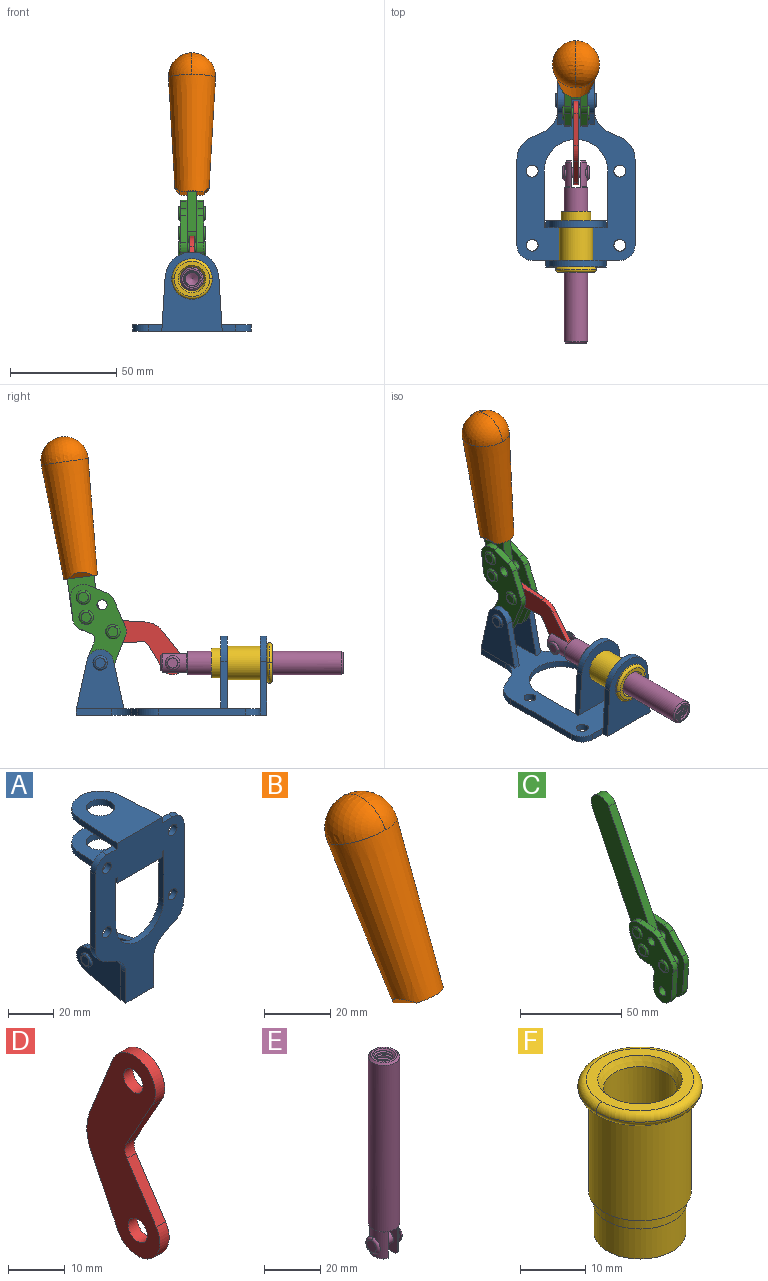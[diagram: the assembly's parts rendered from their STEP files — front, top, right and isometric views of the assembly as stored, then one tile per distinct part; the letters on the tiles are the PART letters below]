
ASSEMBLY  parts=6 mates=7
PART A: 55 faces, bbox 55.7x37.4x89.8 mm
  f0: torus R=2.41mm, axis (-1,0,0), area 15mm2, adj f11,f15,f25
  f1: torus R=2.41mm, axis (-1,0,0), area 15mm2, adj f10,f12,f22
  f2: cylinder r=2.78mm len=5.56mm, axis (0,-1,0), area 54.2mm2, adj f30,f54
  f3: cylinder r=14.99mm len=29.97mm, axis (0,-1,0), area 145.9mm2, adj f30,f49,f53,f54
  f4: cylinder r=2.78mm len=5.56mm, axis (0,-1,0), area 54.2mm2, adj f30,f54
  f5: cylinder r=2.78mm len=5.56mm, axis (0,-1,0), area 54.2mm2, adj f30,f54
  f6: cylinder r=2.78mm len=5.56mm, axis (0,-1,0), area 54.2mm2, adj f30,f54
  f7: cylinder r=6.35mm len=12.7mm, axis (0,0,1), area 123.6mm2, adj f27,f51
  f8: cylinder r=6.35mm len=12.7mm, axis (0,0,-1), area 124.7mm2, adj f21,f35
  f9: cylinder r=2.41mm len=11.18mm, axis (-1,0,0), area 169.4mm2, adj f16,f19
  f10: plane 4.83x4.83mm, normal (1,0,0), area 18.3mm2, adj f1,f12
  f11: plane 4.83x4.83mm, normal (-1,0,0), area 18.3mm2, adj f0,f15
  f12: torus R=2.41mm, axis (-1,0,0), area 15mm2, adj f1,f10,f22
  f13: cylinder r=6.35mm len=12.41mm, axis (1,0,0), area 53.4mm2, adj f18,f19,f22,f23
  f14: cylinder r=6.35mm len=12.41mm, axis (-1,0,0), area 53.4mm2, adj f16,f17,f24,f25
  f15: torus R=2.41mm, axis (-1,0,0), area 15mm2, adj f0,f11,f25
  f16: plane 27.86x22.35mm, normal (1,0,0), area 425.4mm2, adj f9,f14,f17,f24,f30
  f17: plane 22.86x4.97mm, normal (0,0.21,0.98), area 72.5mm2, adj f14,f16,f25,f30
  f18: plane 22.86x4.97mm, normal (0,0.21,0.98), area 72.5mm2, adj f13,f19,f22,f30
  f19: plane 27.86x22.35mm, normal (-1,0,0), area 425.4mm2, adj f9,f13,f18,f23,f30
  f20: cylinder r=12.7mm len=25.35mm, axis (0,0,-1), area 119.8mm2, adj f21,f34,f35,f36
  f21: plane 34.21x28.07mm, normal (0,0,-1), area 702.4mm2, adj f8,f20,f30,f34,f36
  f22: plane 27.96x22.45mm, normal (1,0,0), area 407.2mm2, adj f1,f12,f13,f18,f23,f30,f42,f43
  f23: plane 22.86x4.97mm, normal (0,0.21,-0.98), area 72.5mm2, adj f13,f19,f22,f44
  f24: plane 22.86x4.97mm, normal (0,0.21,-0.98), area 72.5mm2, adj f14,f16,f25,f44
  f25: plane 27.86x22.35mm, normal (-1,0,0), area 407.1mm2, adj f0,f14,f15,f17,f24,f30,f45,f46
  f26: plane 3.1x0.95mm, normal (0,0,-1), area 2.7mm2, adj f30,f49,f50,f54
  f27: plane 34.21x28.07mm, normal (0,0,1), area 702.4mm2, adj f7,f28,f30,f50,f52
  f28: cylinder r=12.7mm len=25.35mm, axis (0,0,1), area 118.8mm2, adj f27,f50,f51,f52
  f29: plane 3.1x0.95mm, normal (0,0,-1), area 2.7mm2, adj f30,f52,f53,f54
  f30: plane 86.54x55.63mm, normal (0,1,0), area 2362.9mm2, adj f2,f3,f4,f5,f6,f16,f17,f18
  f31: plane 40.56x3.1mm, normal (-1,0,0), area 125.7mm2, adj f30,f32,f48,f54
  f32: cylinder r=7.11mm len=7.11mm, axis (0,-1,0), area 34.6mm2, adj f30,f31,f33,f54
  f33: plane 6.67x3.1mm, normal (0,0,1), area 20.4mm2, adj f30,f32,f34,f54
  f34: plane 25.39x3.13mm, normal (-1,0.06,0), area 79.5mm2, adj f20,f21,f33,f35,f54
  f35: plane 37.31x28.45mm, normal (0,0,1), area 789.9mm2, adj f8,f20,f34,f36,f54
  f36: plane 25.39x3.13mm, normal (1,0.06,0), area 79.5mm2, adj f20,f21,f35,f37,f54
  f37: plane 6.67x3.1mm, normal (0,0,1), area 20.4mm2, adj f30,f36,f38,f54
  f38: cylinder r=7.11mm len=7.11mm, axis (0,-1,0), area 34.6mm2, adj f30,f37,f39,f54
  f39: plane 40.56x3.1mm, normal (1,0,0), area 125.7mm2, adj f30,f38,f40,f54
  f40: cylinder r=11.18mm len=10.16mm, axis (0,-1,0), area 39.5mm2, adj f30,f39,f41,f54
  f41: plane 6.09x3.1mm, normal (0.42,0,-0.91), area 20.8mm2, adj f30,f40,f42,f54
  f42: cylinder r=11.18mm len=9.41mm, axis (0,-1,0), area 37.2mm2, adj f22,f30,f41,f43,f54
  f43: plane 16.5x3.1mm, normal (1,0,0), area 51.1mm2, adj f22,f42,f44,f54
  f44: plane 17.37x3.1mm, normal (0,0,-1), area 53.8mm2, adj f23,f24,f30,f43,f45,f54
  f45: plane 16.5x3.1mm, normal (-1,0,0), area 51.1mm2, adj f25,f44,f46,f54
  f46: cylinder r=11.18mm len=9.41mm, axis (0,-1,0), area 37.2mm2, adj f25,f30,f45,f47,f54
  f47: plane 6.09x3.1mm, normal (-0.42,0,-0.91), area 20.8mm2, adj f30,f46,f48,f54
  f48: cylinder r=11.18mm len=10.16mm, axis (0,-1,0), area 39.5mm2, adj f30,f31,f47,f54
  f49: plane 26.54x3.1mm, normal (-1,0,0), area 82.3mm2, adj f3,f26,f30,f54
  f50: plane 25.39x3.1mm, normal (1,0.06,0), area 78.8mm2, adj f26,f27,f28,f51,f54
  f51: plane 37.31x28.45mm, normal (0,0,-1), area 789.9mm2, adj f7,f28,f50,f52,f54
  f52: plane 25.39x3.1mm, normal (-1,0.06,0), area 78.8mm2, adj f27,f28,f29,f51,f54
  f53: plane 26.54x3.1mm, normal (1,0,0), area 82.3mm2, adj f3,f29,f30,f54
  f54: plane 89.66x55.63mm, normal (0,-1,0), area 2678.5mm2, adj f2,f3,f4,f5,f6,f26,f29,f31
PART B: 11 faces, bbox 22.3x42.6x64.5 mm
  f0: sphere r=11.13mm, area 411.4mm2, adj f1,f8
  f1: cone r=11.11mm half-angle=3.3deg, axis (0,0.44,0.9), area 3251.8mm2, adj f0,f7,f8,f9,f10
  f2: cylinder r=6.16mm len=11.7mm, axis (1,0,0), area 89.5mm2, adj f3,f4,f5,f6
  f3: plane 60.23x36.75mm, normal (-1,0,0), area 763.6mm2, adj f2,f4,f6,f10
  f4: plane 51.37x25.05mm, normal (0,0.9,-0.44), area 264.2mm2, adj f2,f3,f5,f10
  f5: plane 60.23x36.75mm, normal (1,0,0), area 763.6mm2, adj f2,f4,f6,f10
  f6: plane 51.37x25.05mm, normal (0,-0.9,0.44), area 264.2mm2, adj f2,f3,f5,f10
  f7: plane 9.95x5.95mm, normal (0.71,-0.31,-0.64), area 25.8mm2, adj f1,f10
  f8: sphere r=11.13mm, area 411.4mm2, adj f0,f1
  f9: plane 9.95x5.95mm, normal (-0.71,-0.31,-0.64), area 25.8mm2, adj f1,f10
  f10: plane 14.27x11.38mm, normal (0,-0.44,-0.9), area 106.7mm2, adj f1,f3,f4,f5,f6,f7,f9
PART C: 59 faces, bbox 12.9x60.2x99.6 mm
  f0: torus R=2.39mm, axis (-1,0,0), area 14.9mm2, adj f20,f43,f51
  f1: torus R=2.39mm, axis (-1,0,0), area 14.9mm2, adj f19,f42,f51
  f2: torus R=2.39mm, axis (-1,0,0), area 14.9mm2, adj f18,f35,f51
  f3: torus R=2.39mm, axis (-1,0,0), area 14.9mm2, adj f14,f17,f23
  f4: torus R=2.39mm, axis (-1,0,0), area 14.9mm2, adj f13,f16,f23
  f5: torus R=2.39mm, axis (-1,0,0), area 14.9mm2, adj f12,f15,f23
  f6: cylinder r=2.39mm len=4.78mm, axis (1,0,0), area 46.5mm2, adj f48,f50,f51
  f7: cylinder r=2.39mm len=4.78mm, axis (1,0,0), area 46.5mm2, adj f50,f51
  f8: cylinder r=6.35mm len=12.68mm, axis (1,0,0), area 61.8mm2, adj f38,f39,f50,f51
  f9: cylinder r=2.39mm len=4.78mm, axis (-1,0,0), area 70.5mm2, adj f46,f50
  f10: cylinder r=2.39mm len=4.78mm, axis (-1,0,0), area 46.5mm2, adj f23,f45,f46
  f11: cylinder r=2.39mm len=4.78mm, axis (-1,0,0), area 46.5mm2, adj f23,f46
  f12: plane 4.78x4.78mm, normal (1,0,0), area 17.9mm2, adj f5,f15
  f13: plane 4.78x4.78mm, normal (1,0,0), area 17.9mm2, adj f4,f16
  f14: plane 4.78x4.78mm, normal (1,0,0), area 17.9mm2, adj f3,f17
  f15: torus R=2.39mm, axis (-1,0,0), area 14.9mm2, adj f5,f12,f23
  f16: torus R=2.39mm, axis (-1,0,0), area 14.9mm2, adj f4,f13,f23
  f17: torus R=2.39mm, axis (-1,0,0), area 14.9mm2, adj f3,f14,f23
  f18: plane 4.78x4.78mm, normal (-1,0,0), area 17.9mm2, adj f2,f35
  f19: plane 4.78x4.78mm, normal (-1,0,0), area 17.9mm2, adj f1,f42
  f20: plane 4.78x4.78mm, normal (-1,0,0), area 17.9mm2, adj f0,f43
  f21: plane 2.26x0.2mm, normal (1,0,0), area 0.2mm2, adj f31,f44
  f22: plane 2.26x0.2mm, normal (-1,0,0), area 0.2mm2, adj f41,f44
  f23: plane 39.37x30.77mm, normal (1,0,0), area 565.5mm2, adj f3,f4,f5,f10,f11,f15,f16,f17
  f24: cylinder r=6.1mm len=4.15mm, axis (-1,0,0), area 14.7mm2, adj f23,f25,f32,f46
  f25: plane 10.25x9.01mm, normal (0,-0.75,0.66), area 42.3mm2, adj f23,f24,f26,f46
  f26: cylinder r=6.35mm len=4.64mm, axis (-1,0,0), area 15.6mm2, adj f23,f25,f27,f46
  f27: plane 15.84x3.1mm, normal (0,-1,-0.07), area 49.2mm2, adj f23,f26,f28,f46
  f28: cylinder r=6.35mm len=12.68mm, axis (-1,0,0), area 61.8mm2, adj f23,f27,f29,f46
  f29: plane 8.11x3.1mm, normal (0,1,0.07), area 25.2mm2, adj f23,f28,f30,f46
  f30: cylinder r=3.05mm len=3.25mm, axis (-1,0,0), area 14.8mm2, adj f23,f29,f31,f46
  f31: plane 5.99x3.1mm, normal (0,0.07,-1), area 18.6mm2, adj f21,f23,f30,f44,f46
  f32: plane 9.5x3.1mm, normal (0,-0.07,1), area 29.5mm2, adj f23,f24,f33,f46,f47
  f33: cylinder r=6.1mm len=8.63mm, axis (-1,0,0), area 39.1mm2, adj f23,f32,f34,f47
  f34: plane 8.65x3.96mm, normal (0,0.91,-0.42), area 29.5mm2, adj f23,f33,f44,f47
  f35: torus R=2.39mm, axis (-1,0,0), area 14.9mm2, adj f2,f18,f51
  f36: plane 10.25x9.01mm, normal (0,-0.75,0.66), area 42.3mm2, adj f37,f49,f50,f51
  f37: cylinder r=6.35mm len=4.64mm, axis (1,0,0), area 15.6mm2, adj f36,f38,f50,f51
  f38: plane 15.84x3.1mm, normal (0,-1,-0.07), area 49.2mm2, adj f8,f37,f50,f51
  f39: plane 8.11x3.1mm, normal (0,1,0.07), area 25.2mm2, adj f8,f40,f50,f51
  f40: cylinder r=3.05mm len=3.25mm, axis (1,0,0), area 14.8mm2, adj f39,f41,f50,f51
  f41: plane 5.99x3.1mm, normal (0,0.07,-1), area 18.6mm2, adj f22,f40,f44,f50,f51
  f42: torus R=2.39mm, axis (-1,0,0), area 14.9mm2, adj f1,f19,f51
  f43: torus R=2.39mm, axis (-1,0,0), area 14.9mm2, adj f0,f20,f51
  f44: cylinder r=6.35mm len=12.12mm, axis (-1,0,0), area 128.9mm2, adj f21,f22,f23,f31,f34,f41,f46,f47
  f45: plane 2.65x1.35mm, normal (1,0,0), area 1mm2, adj f10,f55
  f46: plane 39.08x20.42mm, normal (-1,0,0), area 412.5mm2, adj f9,f10,f11,f24,f25,f26,f27,f28
  f47: plane 77.62x39.82mm, normal (1,0,0), area 850mm2, adj f32,f33,f34,f44,f53,f54,f55
  f48: plane 2.65x1.35mm, normal (-1,0,0), area 1mm2, adj f6,f55
  f49: cylinder r=6.1mm len=4.15mm, axis (1,0,0), area 14.7mm2, adj f36,f50,f51,f56
  f50: plane 39.08x20.42mm, normal (1,0,0), area 412.5mm2, adj f6,f7,f8,f9,f36,f37,f38,f39
  f51: plane 39.37x30.77mm, normal (-1,0,0), area 565.5mm2, adj f0,f1,f2,f6,f7,f8,f35,f36
  f52: plane 8.65x3.96mm, normal (0,0.91,-0.42), area 29.5mm2, adj f44,f51,f57,f58
  f53: plane 68.49x33.4mm, normal (0,0.9,-0.44), area 358.1mm2, adj f44,f47,f54,f58
  f54: cylinder r=6.35mm len=12.06mm, axis (1,0,0), area 93.7mm2, adj f47,f53,f55,f58
  f55: plane 68.49x33.4mm, normal (0,-0.9,0.44), area 358.1mm2, adj f44,f45,f46,f47,f48,f50,f54,f58
  f56: plane 9.5x3.1mm, normal (0,-0.07,1), area 29.5mm2, adj f49,f50,f51,f57,f58
  f57: cylinder r=6.1mm len=8.63mm, axis (1,0,0), area 39.1mm2, adj f51,f52,f56,f58
  f58: plane 77.62x39.82mm, normal (-1,0,0), area 850mm2, adj f44,f52,f53,f54,f55,f56,f57
PART D: 12 faces, bbox 2.3x18.2x42.8 mm
  f0: cylinder r=2.4mm len=4.8mm, axis (1,0,0), area 34.9mm2, adj f4,f11
  f1: cylinder r=10.41mm len=8.47mm, axis (1,0,0), area 20.2mm2, adj f4,f9,f10,f11
  f2: cylinder r=3.05mm len=3.16mm, axis (1,0,0), area 7.7mm2, adj f4,f6,f7,f11
  f3: cylinder r=2.4mm len=4.8mm, axis (1,0,0), area 34.9mm2, adj f4,f11
  f4: plane 42.81x18.23mm, normal (-1,0,0), area 414.1mm2, adj f0,f1,f2,f3,f5,f6,f7,f8
  f5: cylinder r=5.54mm len=10.67mm, axis (1,0,0), area 41.8mm2, adj f4,f6,f10,f11
  f6: plane 11.66x6.53mm, normal (0,-0.87,-0.49), area 30.9mm2, adj f2,f4,f5,f11
  f7: plane 11.17x7.33mm, normal (0,-0.84,0.55), area 30.9mm2, adj f2,f4,f8,f11
  f8: cylinder r=5.54mm len=10.51mm, axis (1,0,0), area 41.8mm2, adj f4,f7,f9,f11
  f9: plane 13.67x6.67mm, normal (0,0.9,-0.44), area 35.1mm2, adj f1,f4,f8,f11
  f10: plane 14.1x5.7mm, normal (0,0.93,0.37), area 35.1mm2, adj f1,f4,f5,f11
  f11: plane 42.81x18.23mm, normal (1,0,0), area 414.1mm2, adj f0,f1,f2,f3,f5,f6,f7,f8
PART E: 48 faces, bbox 12.6x11.1x86.1 mm
  f0: torus R=2.41mm, axis (-1,0,0), area 15mm2, adj f30,f32,f34
  f1: torus R=2.41mm, axis (-1,0,0), area 15mm2, adj f29,f31,f33
  f2: cylinder r=5.54mm len=72.39mm, axis (0,0,1), area 2518.5mm2, adj f3,f4,f42,f43
  f3: cone r=5.54mm half-angle=45deg, axis (0,0,1), area 7.6mm2, adj f2,f5,f41
  f4: cone r=5.54mm half-angle=45deg, axis (0,0,-1), area 34.9mm2, adj f2,f39
  f5: cylinder r=5.08mm len=11.48mm, axis (0,0,1), area 108.3mm2, adj f3,f7,f8,f41
  f6: cylinder r=2.41mm len=4.83mm, axis (-1,0,0), area 71.2mm2, adj f40,f41
  f7: cylinder r=2.41mm len=4.83mm, axis (-1,0,0), area 7.6mm2, adj f5,f34
  f8: cone r=5.08mm half-angle=45deg, axis (0,0,1), area 10.6mm2, adj f5,f37,f41
  f9: cone r=3.98mm half-angle=45deg, axis (0,0,1), area 17.6mm2, adj f27,f39,f45,f46,f47
  f10: cylinder r=2.41mm len=4.83mm, axis (-1,0,0), area 7.6mm2, adj f33,f38
  f11: cylinder r=3.2mm len=6.4mm, axis (0,0,1), area 78.4mm2, adj f12,f28,f44,f45,f47
  f12: cylinder r=3.2mm len=6.4mm, axis (0,0,1), area 10.5mm2, adj f11,f13,f45,f47
  f13: cylinder r=3.2mm len=6.4mm, axis (0,0,1), area 10.5mm2, adj f12,f14,f45,f47
  f14: cylinder r=3.2mm len=6.4mm, axis (0,0,1), area 10.5mm2, adj f13,f15,f45,f47
  f15: cylinder r=3.2mm len=6.4mm, axis (0,0,1), area 10.5mm2, adj f14,f16,f45,f47
  f16: cylinder r=3.2mm len=6.4mm, axis (0,0,1), area 10.5mm2, adj f15,f17,f45,f47
  f17: cylinder r=3.2mm len=6.4mm, axis (0,0,1), area 10.5mm2, adj f16,f18,f45,f47
  f18: cylinder r=3.2mm len=6.4mm, axis (0,0,1), area 10.5mm2, adj f17,f19,f45,f47
  f19: cylinder r=3.2mm len=6.4mm, axis (0,0,1), area 10.5mm2, adj f18,f20,f45,f47
  f20: cylinder r=3.2mm len=6.4mm, axis (0,0,1), area 10.5mm2, adj f19,f21,f45,f47
  f21: cylinder r=3.2mm len=6.4mm, axis (0,0,1), area 10.5mm2, adj f20,f22,f45,f47
  f22: cylinder r=3.2mm len=6.4mm, axis (0,0,1), area 10.5mm2, adj f21,f23,f45,f47
  f23: cylinder r=3.2mm len=6.4mm, axis (0,0,1), area 10.5mm2, adj f22,f24,f45,f47
  f24: cylinder r=3.2mm len=6.4mm, axis (0,0,1), area 10.5mm2, adj f23,f25,f45,f47
  f25: cylinder r=3.2mm len=6.4mm, axis (0,0,1), area 10.5mm2, adj f24,f26,f45,f47
  f26: cylinder r=3.2mm len=6.4mm, axis (0,0,1), area 10.5mm2, adj f25,f27,f45,f47
  f27: cylinder r=3.2mm len=6.4mm, axis (0,0,1), area 7.4mm2, adj f9,f26,f45,f47
  f28: cone r=3.2mm half-angle=60deg, axis (0,0,1), area 37.2mm2, adj f11
  f29: plane 4.83x4.83mm, normal (-1,0,0), area 18.3mm2, adj f1,f31
  f30: plane 4.83x4.83mm, normal (1,0,0), area 18.3mm2, adj f0,f32
  f31: torus R=2.41mm, axis (-1,0,0), area 15mm2, adj f1,f29,f33
  f32: torus R=2.41mm, axis (-1,0,0), area 15mm2, adj f0,f30,f34
  f33: plane 6.83x6.83mm, normal (1,0,0), area 18.3mm2, adj f1,f10,f31
  f34: plane 6.83x6.83mm, normal (-1,0,0), area 18.3mm2, adj f0,f7,f32
  f35: cone r=5.08mm half-angle=45deg, axis (0,0,1), area 10.6mm2, adj f36,f38,f40
  f36: plane 7.25x1.97mm, normal (0,0,-1), area 10mm2, adj f35,f40
  f37: plane 7.25x1.97mm, normal (0,0,-1), area 10mm2, adj f8,f41
  f38: cylinder r=5.08mm len=11.48mm, axis (0,0,1), area 108.3mm2, adj f10,f35,f40,f42
  f39: plane 9.55x9.55mm, normal (0,0,1), area 22mm2, adj f4,f9
  f40: plane 12.76x10.09mm, normal (1,0,0), area 95.7mm2, adj f6,f35,f36,f38,f42,f43
  f41: plane 12.76x10.09mm, normal (-1,0,0), area 95.7mm2, adj f3,f5,f6,f8,f37,f43
  f42: cone r=5.54mm half-angle=45deg, axis (0,0,1), area 7.6mm2, adj f2,f38,f40
  f43: plane 11.07x4.7mm, normal (0,0,-1), area 50.4mm2, adj f2,f40,f41
  f44: plane 0.89x0.62mm, normal (-1,0,0), area 0.3mm2, adj f11,f45,f46,f47
  f45: bspline ~24.8x7.63mm, area 266.6mm2, adj f9,f11,f12,f13,f14,f15,f16,f17
  f46: bspline ~24.87x7.63mm, area 73.6mm2, adj f9,f44,f45,f47
  f47: bspline ~24.98x7.63mm, area 272.5mm2, adj f9,f11,f12,f13,f14,f15,f16,f17
PART F: 15 faces, bbox 20.6x20.6x28.7 mm
  f0: torus R=8.26mm, axis (0,0,1), area 56.8mm2, adj f1,f10,f12
  f1: torus R=8.26mm, axis (0,0,1), area 56.8mm2, adj f0,f6,f13
  f2: cylinder r=5.59mm len=25.91mm, axis (0,0,1), area 909.6mm2, adj f3,f4
  f3: cone r=6.86mm half-angle=45deg, axis (0,0,-1), area 70.2mm2, adj f2,f14
  f4: cone r=6.47mm half-angle=30deg, axis (0,0,1), area 66.7mm2, adj f2,f13
  f5: cylinder r=7.04mm len=14.07mm, axis (0,0,1), area 252.6mm2, adj f11,f14
  f6: torus R=8.26mm, axis (0,0,1), area 56.8mm2, adj f1,f12,f13
  f7: cylinder r=7.16mm len=14.33mm, axis (0,0,1), area 91.5mm2, adj f9,f11
  f8: cylinder r=7.86mm len=18.42mm, axis (0,0,1), area 909.6mm2, adj f9,f10
  f9: plane 15.72x15.72mm, normal (0,0,-1), area 33mm2, adj f7,f8
  f10: plane 16.51x16.51mm, normal (0,0,-1), area 19.9mm2, adj f0,f8,f12
  f11: plane 14.33x14.33mm, normal (0,0,-1), area 5.7mm2, adj f5,f7
  f12: torus R=8.26mm, axis (0,0,1), area 56.8mm2, adj f0,f6,f10
  f13: plane 16.51x16.51mm, normal (0,0,1), area 82.7mm2, adj f1,f4,f6
  f14: plane 14.07x14.07mm, normal (0,0,-1), area 7.8mm2, adj f3,f5
PLACE A rot(axis=(1,0,0),90deg) t=(0,9.14,0)mm fixed
PLACE B rot(axis=(0,0.29,0.96),180deg) t=(0,86.77,36.59)mm
PLACE C rot(axis=(1,0,0),18.2deg) t=(0,7.84,47.42)mm
PLACE D rot(axis=(1,0,0),119.6deg) t=(0,32.7,10.85)mm
PLACE E rot(axis=(1,0,0),90deg) t=(0,22.57,0)mm
PLACE F rot(axis=(1,0,0),90deg) t=(0,9.14,0)mm
MATE fastened F.f2 <-> A.f7  axis (0,1,0) through (0,-37.25,24.61)mm
MATE revolute C.f7 <-> A.f0  axis (-1,0,0) through (0,41.23,24.61)mm
MATE parallel B.f4 <-> C.f53  axis (0,-0.99,0.14) through (0,56.57,64.17)mm
MATE revolute B.f2 <-> C.f54  axis (-1,0,0) through (0,58.24,121.63)mm
MATE revolute D.f3 <-> C.f4  axis (1,0,0) through (0,35.24,39.31)mm
MATE slider E.f2 <-> F.f2  axis (0,-1,0) through (0,-36.21,24.61)mm
MATE revolute D.f5 <-> E.f6  axis (1,0,0) through (0,7.1,24.61)mm
